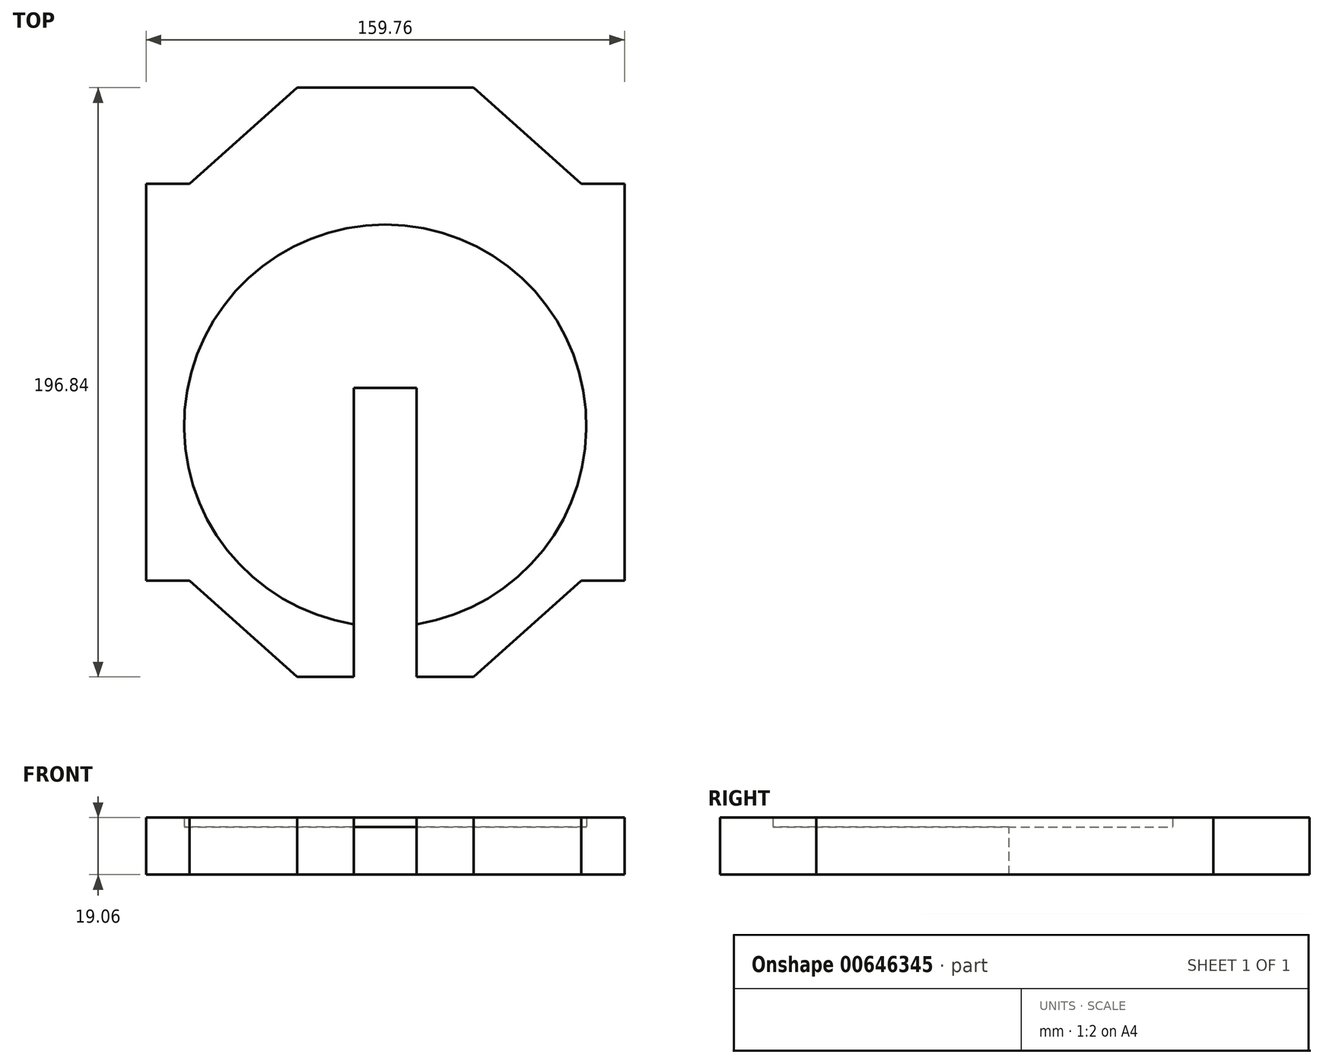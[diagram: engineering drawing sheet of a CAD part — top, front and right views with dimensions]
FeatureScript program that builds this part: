
annotation { "Feature Type Name" : "Feature", "Feature Type Description" : "" }
export const myFeature = defineFeature(function(context is Context, id is Id, definition is map)
    precondition{}
    {
        {
            var Q0;
            Q0=qCreatedBy(makeId("Top.planeOp"),FACE);
            var sketch = newSketch(context, id + "F0", { "sketchPlane" : qUnion([Q0])});
            skLineSegment(sketch, "E0.bottom", {"start": v(29.46, 98.42) * mm, "end": v(-29.46, 98.42) * mm});
            skLineSegment(sketch, "E0.top", {"start": v(29.46, -98.42) * mm, "end": v(-29.46, -98.42) * mm});
            skLineSegment(sketch, "E0.left", {"start": v(29.46, 98.42) * mm, "end": v(29.46, -98.42) * mm});
            skLineSegment(sketch, "E0.right", {"start": v(-29.46, 98.42) * mm, "end": v(-29.46, -98.42) * mm});
            skPoint(sketch, "E0.middle", {"position": v(0, 0) * mm});
            skLineSegment(sketch, "E1.bottom", {"start": v(-65.4, 66.3) * mm, "end": v(65.4, 66.3) * mm});
            skLineSegment(sketch, "E1.top", {"start": v(-65.4, -66.3) * mm, "end": v(65.4, -66.3) * mm});
            skLineSegment(sketch, "E1.left", {"start": v(-65.4, 66.3) * mm, "end": v(-65.4, -66.3) * mm});
            skLineSegment(sketch, "E1.right", {"start": v(65.4, 66.3) * mm, "end": v(65.4, -66.3) * mm});
            skLineSegment(sketch, "E2", {"start": v(-29.46, -98.42) * mm, "end": v(-65.4, -66.3) * mm});
            skLineSegment(sketch, "E3", {"start": v(29.46, -98.42) * mm, "end": v(65.4, -66.3) * mm});
            skLineSegment(sketch, "E4", {"start": v(65.4, 66.3) * mm, "end": v(29.46, 98.42) * mm});
            skLineSegment(sketch, "E5", {"start": v(-65.4, 66.3) * mm, "end": v(-29.46, 98.42) * mm});
            skLineSegment(sketch, "E6.bottom", {"start": v(-79.88, 66.3) * mm, "end": v(79.88, 66.3) * mm});
            skLineSegment(sketch, "E6.top", {"start": v(-79.88, -66.3) * mm, "end": v(79.88, -66.3) * mm});
            skLineSegment(sketch, "E6.left", {"start": v(-79.88, 66.3) * mm, "end": v(-79.88, -66.3) * mm});
            skLineSegment(sketch, "E6.right", {"start": v(79.88, 66.3) * mm, "end": v(79.88, -66.3) * mm});
            skSolve(sketch);
        }
        {
            var Q0;
            Q0=qCreatedBy(makeId("Top.planeOp"),FACE);
            var sketch = newSketch(context, id + "F1", { "sketchPlane" : qUnion([Q0])});
            skSolve(sketch);
        }
        {
            var Q0;
            {var subQ0=sQuery(id+"F0.wireOp",EDGE,"E0.bottom");Q0=makeQuery(id+"F0.imprint","IMPRINT",FACE,{"disambiguationData":[TD([[makeQuery(id+"F0.imprint","IMPRINT",EDGE,{"derivedFrom":subQ0}),1.0]])]});}
            var Q1;
            {var subQ5=sQuery(id+"F0.wireOp",EDGE,"E1.left");Q1=makeQuery(id+"F0.imprint","IMPRINT",FACE,{"disambiguationData":[TD([[makeQuery(id+"F0.imprint","IMPRINT",EDGE,{"derivedFrom":subQ5}),1.0]])]});}
            var Q2;
            {var subQ0=sQuery(id+"F0.wireOp",EDGE,"E5");Q2=makeQuery(id+"F0.imprint","IMPRINT",FACE,{"disambiguationData":[TD([[makeQuery(id+"F0.imprint","IMPRINT",EDGE,{"derivedFrom":subQ0}),-1.0]])]});}
            var Q3;
            {var subQ0=sQuery(id+"F0.wireOp",EDGE,"E1.bottom");var subQ1=sQuery(id+"F0.wireOp",EDGE,"E0.left");var subQ2=makeQuery(id+"F0.imprint","INTERSECT",VERTEX,{"derivedFrom":[subQ1,subQ0]});Q3=makeQuery(id+"F0.imprint","IMPRINT",FACE,{"disambiguationData":[TD([[makeQuery(id+"F0.imprint","IMPRINT",EDGE,{"disambiguationData":[TD([[subQ2,-1.0]])],"derivedFrom":subQ1}),-1.0]])]});}
            var Q4;
            {var subQ5=sQuery(id+"F0.wireOp",EDGE,"E1.right");Q4=makeQuery(id+"F0.imprint","IMPRINT",FACE,{"disambiguationData":[TD([[makeQuery(id+"F0.imprint","IMPRINT",EDGE,{"derivedFrom":subQ5}),-1.0]])]});}
            var Q5;
            {var subQ0=sQuery(id+"F0.wireOp",EDGE,"E4");Q5=makeQuery(id+"F0.imprint","IMPRINT",FACE,{"disambiguationData":[TD([[makeQuery(id+"F0.imprint","IMPRINT",EDGE,{"derivedFrom":subQ0}),1.0]])]});}
            var Q6;
            {var subQ0=sQuery(id+"F0.wireOp",EDGE,"E3");Q6=makeQuery(id+"F0.imprint","IMPRINT",FACE,{"disambiguationData":[TD([[makeQuery(id+"F0.imprint","IMPRINT",EDGE,{"derivedFrom":subQ0}),1.0]])]});}
            var Q7;
            {var subQ0=sQuery(id+"F0.wireOp",EDGE,"E0.top");Q7=makeQuery(id+"F0.imprint","IMPRINT",FACE,{"disambiguationData":[TD([[makeQuery(id+"F0.imprint","IMPRINT",EDGE,{"derivedFrom":subQ0}),-1.0]])]});}
            var Q8;
            {var subQ0=sQuery(id+"F0.wireOp",EDGE,"E2");Q8=makeQuery(id+"F0.imprint","IMPRINT",FACE,{"disambiguationData":[TD([[makeQuery(id+"F0.imprint","IMPRINT",EDGE,{"derivedFrom":subQ0}),-1.0]])]});}
            var Q9;
            Q9 = qSketchRegion(id + "F1", true);
            var Q10;
            {var subQ0=sQuery(id+"F0.wireOp",EDGE,"E1.left");Q10=makeQuery(id+"F0.imprint","IMPRINT",FACE,{"disambiguationData":[TD([[makeQuery(id+"F0.imprint","IMPRINT",EDGE,{"derivedFrom":subQ0}),-1.0]])]});}
            var Q11;
            {var subQ0=sQuery(id+"F0.wireOp",EDGE,"E1.right");Q11=makeQuery(id+"F0.imprint","IMPRINT",FACE,{"disambiguationData":[TD([[makeQuery(id+"F0.imprint","IMPRINT",EDGE,{"derivedFrom":subQ0}),1.0]])]});}
            extrude(context, id + "F2", {"entities" : qUnion([Q0, Q1, Q2, Q3, Q4, Q5, Q6, Q7, Q8, Q9, Q10, Q11]), "endBound" : BoundingType.SYMMETRIC, "depth" : 19.05 * mm, "offsetDistance" : 25.4 * mm});
        }
        {
            var Q0;
            Q0=qCreatedBy(makeId("Top.planeOp"),FACE);
            var sketch = newSketch(context, id + "F3", { "sketchPlane" : qUnion([Q0])});
            skLineSegment(sketch, "E7", {"start": v(-10.48, -98.42) * mm, "end": v(10.48, -98.42) * mm});
            skLineSegment(sketch, "E8", {"start": v(-10.48, -98.42) * mm, "end": v(-10.48, -1.9) * mm});
            skLineSegment(sketch, "E9", {"start": v(-10.48, -1.9) * mm, "end": v(10.48, -1.9) * mm});
            skLineSegment(sketch, "E10", {"start": v(10.48, -1.9) * mm, "end": v(10.48, -98.42) * mm});
            skSolve(sketch);
        }
        {
            var Q0;
            Q0=qSketchRegion(id+"F3",true);
            extrude(context, id + "F4", {"entities" : qUnion([Q0]), "operationType" : NewBodyOperationType.REMOVE, "endBound" : BoundingType.SYMMETRIC, "oppositeDirection" : true, "depth" : 19.05 * mm, "offsetDistance" : 25.4 * mm});
        }
        {
            var Q0;
            Q0=qCreatedBy(makeId("Top.planeOp"),FACE);
            cPlane(context, id + "F5", {"entities" : qUnion([Q0]), "cplaneType" : CPlaneType.OFFSET, "offset" : 6.35 * mm, "width" : 152.4 * mm, "height" : 152.4 * mm});
        }
        {
            var Q0;
            Q0=qCreatedBy(id+"F5.planeOp",FACE);
            var sketch = newSketch(context, id + "F6", { "sketchPlane" : qUnion([Q0])});
            skCircle(sketch, "E11", {"center": v(0, -14.48) * mm, "radius": 67.18 * mm});
            skSolve(sketch);
        }
        {
            var Q0;
            Q0 = qSketchRegion(id + "F6", true);
            var Q1;
            Q1=makeQuery(id+"F2.opExtrude","CAP_FACE",FACE,{"disambiguationData":[OSD([sQuery(id+"F0.wireOp",EDGE,"E0.bottom"),sQuery(id+"F0.wireOp",EDGE,"E0.top"),sQuery(id+"F0.wireOp",EDGE,"E2"),sQuery(id+"F0.wireOp",EDGE,"E3"),sQuery(id+"F0.wireOp",EDGE,"E4"),sQuery(id+"F0.wireOp",EDGE,"E5"),sQuery(id+"F0.wireOp",EDGE,"E6.bottom"),sQuery(id+"F0.wireOp",EDGE,"E6.top"),sQuery(id+"F0.wireOp",EDGE,"E6.left"),sQuery(id+"F0.wireOp",EDGE,"E6.right")])],"isStart":false});
            extrude(context, id + "F7", {"entities" : qUnion([Q0, Q1]), "operationType" : NewBodyOperationType.REMOVE, "depth" : 6.35 * mm, "offsetDistance" : 25.4 * mm});
        }
    });
